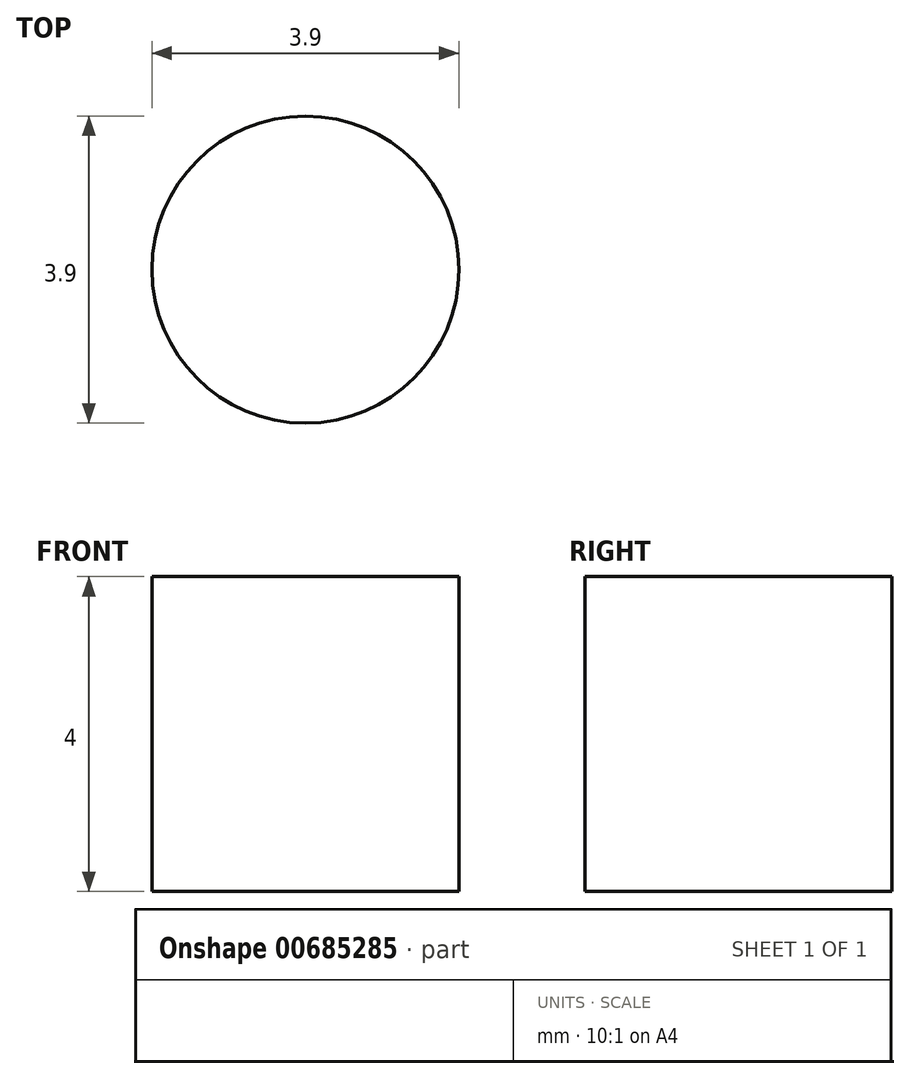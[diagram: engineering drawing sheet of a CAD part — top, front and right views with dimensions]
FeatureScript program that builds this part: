
annotation { "Feature Type Name" : "Feature", "Feature Type Description" : "" }
export const myFeature = defineFeature(function(context is Context, id is Id, definition is map)
    precondition{}
    {
        {
            var Q0;
            Q0=qCreatedBy(makeId("Top.planeOp"),FACE);
            var sketch = newSketch(context, id + "F0", { "sketchPlane" : qUnion([Q0])});
            skCircle(sketch, "E0", {"center": v(0, 0) * mm, "radius": 1.95 * mm});
            skSolve(sketch);
        }
        {
            var Q0;
            Q0=makeQuery(id+"F0.imprint","IMPRINT",FACE,{"disambiguationData":[TD([[makeQuery(id+"F0.imprint","IMPRINT",EDGE,{"derivedFrom":sQuery(id+"F0.wireOp",EDGE,"E0")}),1.0]])]});
            extrude(context, id + "F1", {"entities" : qUnion([Q0]), "depth" : 4 * mm, "offsetDistance" : 25 * mm});
        }
    });
